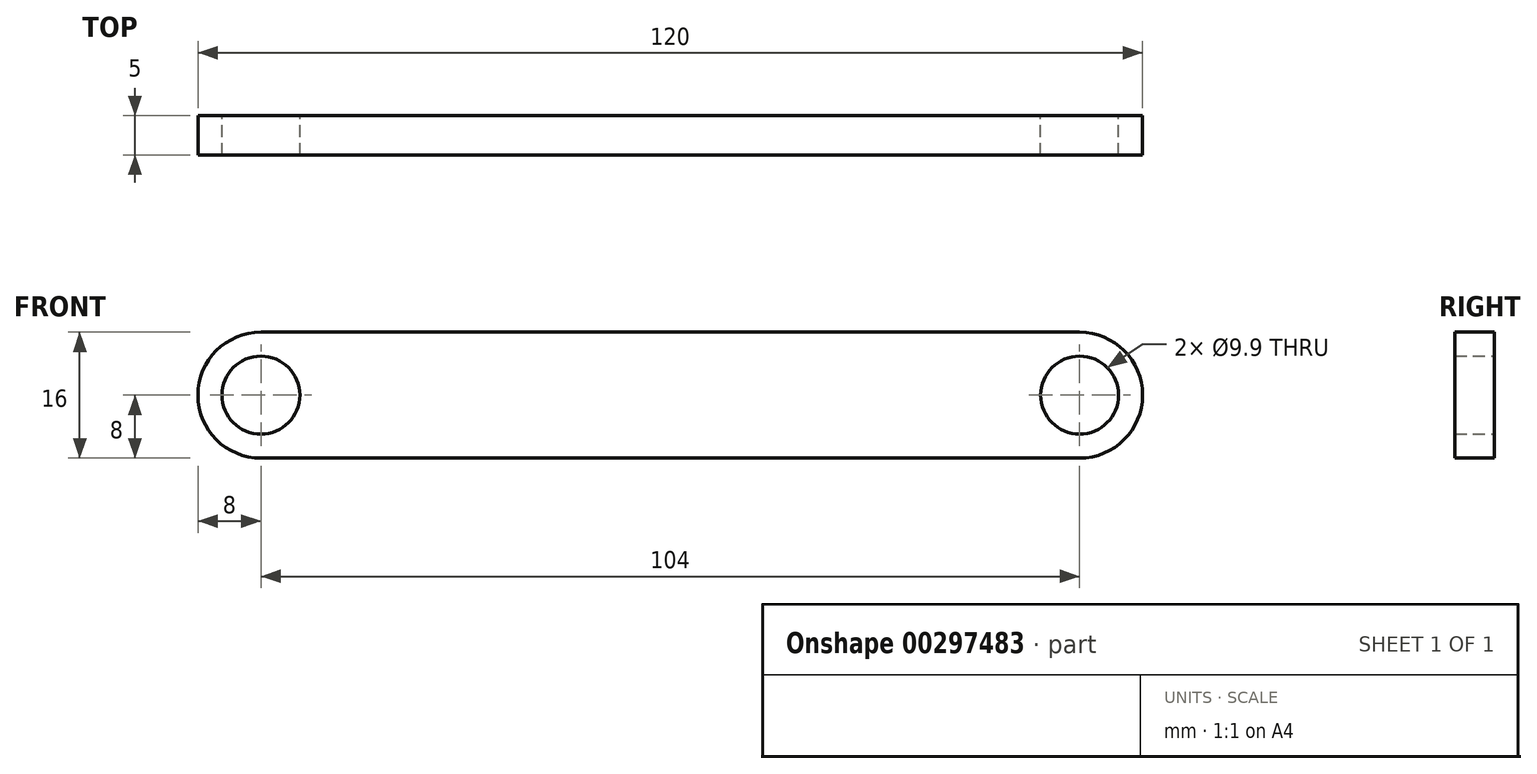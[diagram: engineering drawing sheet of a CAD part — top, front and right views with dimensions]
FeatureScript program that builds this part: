
annotation { "Feature Type Name" : "Feature", "Feature Type Description" : "" }
export const myFeature = defineFeature(function(context is Context, id is Id, definition is map)
    precondition{}
    {
        {
            var Q0;
            Q0=qCreatedBy(makeId("Front.planeOp"),FACE);
            var sketch = newSketch(context, id + "F0", { "sketchPlane" : qUnion([Q0])});
            skLineSegment(sketch, "E0.bottom", {"start": v(52, -8) * mm, "end": v(-52, -8) * mm});
            skLineSegment(sketch, "E0.top", {"start": v(52, 8) * mm, "end": v(-52, 8) * mm});
            skLineSegment(sketch, "E0.left", {"start": v(60, 0) * mm, "end": v(60, 0) * mm});
            skLineSegment(sketch, "E0.right", {"start": v(-60, 0) * mm, "end": v(-60, 0) * mm});
            skPoint(sketch, "E0.middle", {"position": v(0, 0) * mm});
            skCircle(sketch, "E1", {"center": v(-52, 0) * mm, "radius": 4.95 * mm});
            skCircle(sketch, "E2.MirrorC", {"center": v(52, 0) * mm, "radius": 4.95 * mm});
            skPoint(sketch, "E3.visualSharp", {"position": v(-60, 8) * mm});
            skArc(sketch, "E3.filletArc", {"start": v(-52, 8) * mm, "mid": v(-57.66, 5.66) * mm, "end": v(-60, 0) * mm});
            skPoint(sketch, "E4.visualSharp", {"position": v(-60, -8) * mm});
            skArc(sketch, "E4.filletArc", {"start": v(-60, 0) * mm, "mid": v(-57.66, -5.66) * mm, "end": v(-52, -8) * mm});
            skPoint(sketch, "E5.visualSharp", {"position": v(60, 8) * mm});
            skArc(sketch, "E5.filletArc", {"start": v(60, 0) * mm, "mid": v(57.66, 5.66) * mm, "end": v(52, 8) * mm});
            skPoint(sketch, "E6.visualSharp", {"position": v(60, -8) * mm});
            skArc(sketch, "E6.filletArc", {"start": v(52, -8) * mm, "mid": v(57.66, -5.66) * mm, "end": v(60, 0) * mm});
            skSolve(sketch);
        }
        {
            var Q0;
            Q0=makeQuery(id+"F0.imprint","IMPRINT",FACE,{"disambiguationData":[TD([[makeQuery(id+"F0.imprint","IMPRINT",EDGE,{"derivedFrom":sQuery(id+"F0.wireOp",EDGE,"E0.bottom")}),-1.0]])]});
            extrude(context, id + "F1", {"entities" : qUnion([Q0]), "depth" : 5 * mm});
        }
    });
